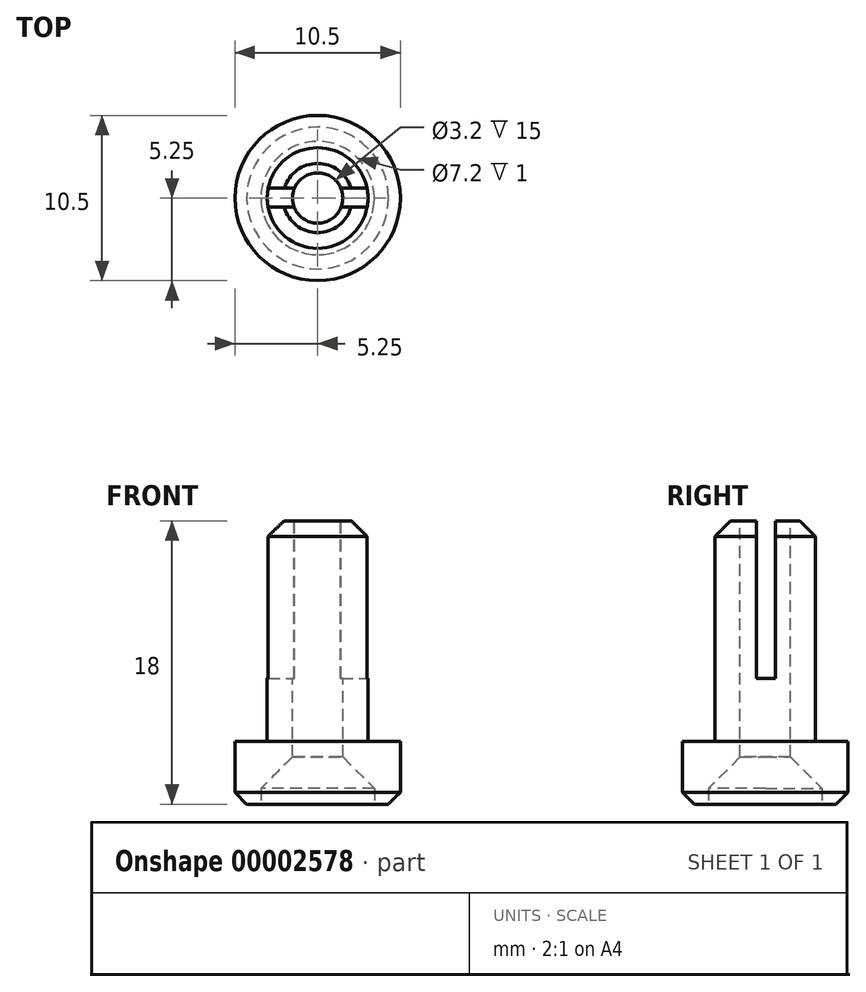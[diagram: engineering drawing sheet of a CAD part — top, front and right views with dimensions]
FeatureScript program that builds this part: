
annotation { "Feature Type Name" : "Feature", "Feature Type Description" : "" }
export const myFeature = defineFeature(function(context is Context, id is Id, definition is map)
    precondition{}
    {
        {
            var Q0;
            Q0=qCreatedBy(makeId("Top.planeOp"),FACE);
            var sketch = newSketch(context, id + "F0", { "sketchPlane" : qUnion([Q0])});
            skCircle(sketch, "E0", {"center": v(0, 0) * mm, "radius": 5.25 * mm});
            skSolve(sketch);
        }
        {
            var Q0;
            Q0=makeQuery(id+"F0.imprint","IMPRINT",FACE,{"disambiguationData":[TD([[makeQuery(id+"F0.imprint","IMPRINT",EDGE,{"derivedFrom":sQuery(id+"F0.wireOp",EDGE,"E0")}),1.0]])]});
            extrude(context, id + "F1", {"entities" : qUnion([Q0]), "depth" : 4 * mm});
        }
        {
            var Q0;
            Q0=makeQuery(id+"F0.imprint","IMPRINT",FACE,{"disambiguationData":[TD([[makeQuery(id+"F0.imprint","IMPRINT",EDGE,{"derivedFrom":sQuery(id+"F0.wireOp",EDGE,"E0")}),1.0]])]});
            var sketch = newSketch(context, id + "F2", { "sketchPlane" : qUnion([Q0])});
            skCircle(sketch, "E1", {"center": v(0, 0) * mm, "radius": 3.6 * mm});
            skSolve(sketch);
        }
        {
            var Q0;
            Q0=makeQuery(id+"F2.imprint","IMPRINT",FACE,{"disambiguationData":[TD([[makeQuery(id+"F2.imprint","IMPRINT",EDGE,{"derivedFrom":sQuery(id+"F2.wireOp",EDGE,"E1")}),1.0]])]});
            extrude(context, id + "F3", {"entities" : qUnion([Q0]), "operationType" : NewBodyOperationType.REMOVE, "depth" : 3 * mm});
        }
        {
            var Q0;
            Q0=makeQuery(id+"F1.opExtrude","CAP_FACE",FACE,{"disambiguationData":[OSD([sQuery(id+"F0.wireOp",EDGE,"E0")])],"isStart":false});
            var sketch = newSketch(context, id + "F4", { "sketchPlane" : qUnion([Q0])});
            skCircle(sketch, "E2", {"center": v(0, 0) * mm, "radius": 3.2 * mm});
            skSolve(sketch);
        }
        {
            var Q0;
            Q0=makeQuery(id+"F4.imprint","IMPRINT",FACE,{"disambiguationData":[TD([[makeQuery(id+"F4.imprint","IMPRINT",EDGE,{"derivedFrom":sQuery(id+"F4.wireOp",EDGE,"E2")}),1.0]])]});
            extrude(context, id + "F5", {"entities" : qUnion([Q0]), "operationType" : NewBodyOperationType.ADD, "depth" : 14 * mm});
        }
        {
            var Q0;
            Q0=makeQuery(id+"F1.opExtrude","CAP_EDGE",EDGE,{"disambiguationData":[OSD([sQuery(id+"F0.wireOp",EDGE,"E0")])],"isStart":true});
            chamfer(context, id + "F6", {"entities" : qUnion([Q0]), "width" : .75 * mm, "tangentPropagation" : true});
        }
        {
            var Q0;
            Q0=makeQuery(id+"F3.boolean.opBoolean","COPY",EDGE,{"derivedFrom":makeQuery(id+"F3.opExtrude","CAP_EDGE",EDGE,{"disambiguationData":[OSD([sQuery(id+"F2.wireOp",EDGE,"E1")])],"isStart":false})});
            chamfer(context, id + "F7", {"entities" : qUnion([Q0]), "width" : 2 * mm, "tangentPropagation" : true});
        }
        {
            var Q0;
            Q0=makeQuery(id+"F5.opExtrude","CAP_FACE",FACE,{"disambiguationData":[OSD([sQuery(id+"F4.wireOp",EDGE,"E2")])],"isStart":false});
            var sketch = newSketch(context, id + "F8", { "sketchPlane" : qUnion([Q0])});
            skCircle(sketch, "E3", {"center": v(0, 0) * mm, "radius": 1.6 * mm});
            skSolve(sketch);
        }
        {
            var Q0;
            Q0=qSketchRegion(id+"F8",true);
            extrude(context, id + "F9", {"entities" : qUnion([Q0]), "operationType" : NewBodyOperationType.REMOVE, "endBound" : BoundingType.THROUGH_ALL, "oppositeDirection" : true, "depth" : 25 * mm});
        }
        {
            var Q0;
            Q0=makeQuery(id+"F5.opExtrude","CAP_FACE",FACE,{"disambiguationData":[OSD([sQuery(id+"F4.wireOp",EDGE,"E2")])],"isStart":false});
            var sketch = newSketch(context, id + "F10", { "sketchPlane" : qUnion([Q0])});
            skLineSegment(sketch, "E4.bottom", {"start": v(-5.54, 0.64) * mm, "end": v(5.3, 0.64) * mm});
            skLineSegment(sketch, "E4.top", {"start": v(-5.54, -0.56) * mm, "end": v(5.3, -0.56) * mm});
            skLineSegment(sketch, "E4.left", {"start": v(-5.54, 0.64) * mm, "end": v(-5.54, -0.56) * mm});
            skLineSegment(sketch, "E4.right", {"start": v(5.3, 0.64) * mm, "end": v(5.3, -0.56) * mm});
            skSolve(sketch);
        }
        {
            var Q0;
            Q0=qSketchRegion(id+"F10",true);
            extrude(context, id + "F11", {"entities" : qUnion([Q0]), "operationType" : NewBodyOperationType.REMOVE, "oppositeDirection" : true, "depth" : 10 * mm});
        }
        {
            var Q0;
            {var subQ0=sQuery(id+"F4.wireOp",EDGE,"E2");Q0=makeQuery(id+"F11.boolean.opBoolean","SPLIT",EDGE,{"disambiguationData":[TD([makeQuery(id+"F11.opExtrude","SWEPT_FACE",FACE,{"disambiguationData":[OSD([sQuery(id+"F10.wireOp",EDGE,"E4.top")])]})])],"derivedFrom":makeQuery(id+"F5.opExtrude","CAP_EDGE",EDGE,{"disambiguationData":[OSD([subQ0])],"isStart":false})});}
            var Q1;
            {var subQ0=sQuery(id+"F4.wireOp",EDGE,"E2");Q1=makeQuery(id+"F11.boolean.opBoolean","SPLIT",EDGE,{"disambiguationData":[TD([makeQuery(id+"F11.opExtrude","SWEPT_FACE",FACE,{"disambiguationData":[OSD([sQuery(id+"F10.wireOp",EDGE,"E4.bottom")])]})])],"derivedFrom":makeQuery(id+"F5.opExtrude","CAP_EDGE",EDGE,{"disambiguationData":[OSD([subQ0])],"isStart":false})});}
            chamfer(context, id + "F12", {"entities" : qUnion([Q0, Q1]), "width" : 1 * mm, "tangentPropagation" : true});
        }
    });
